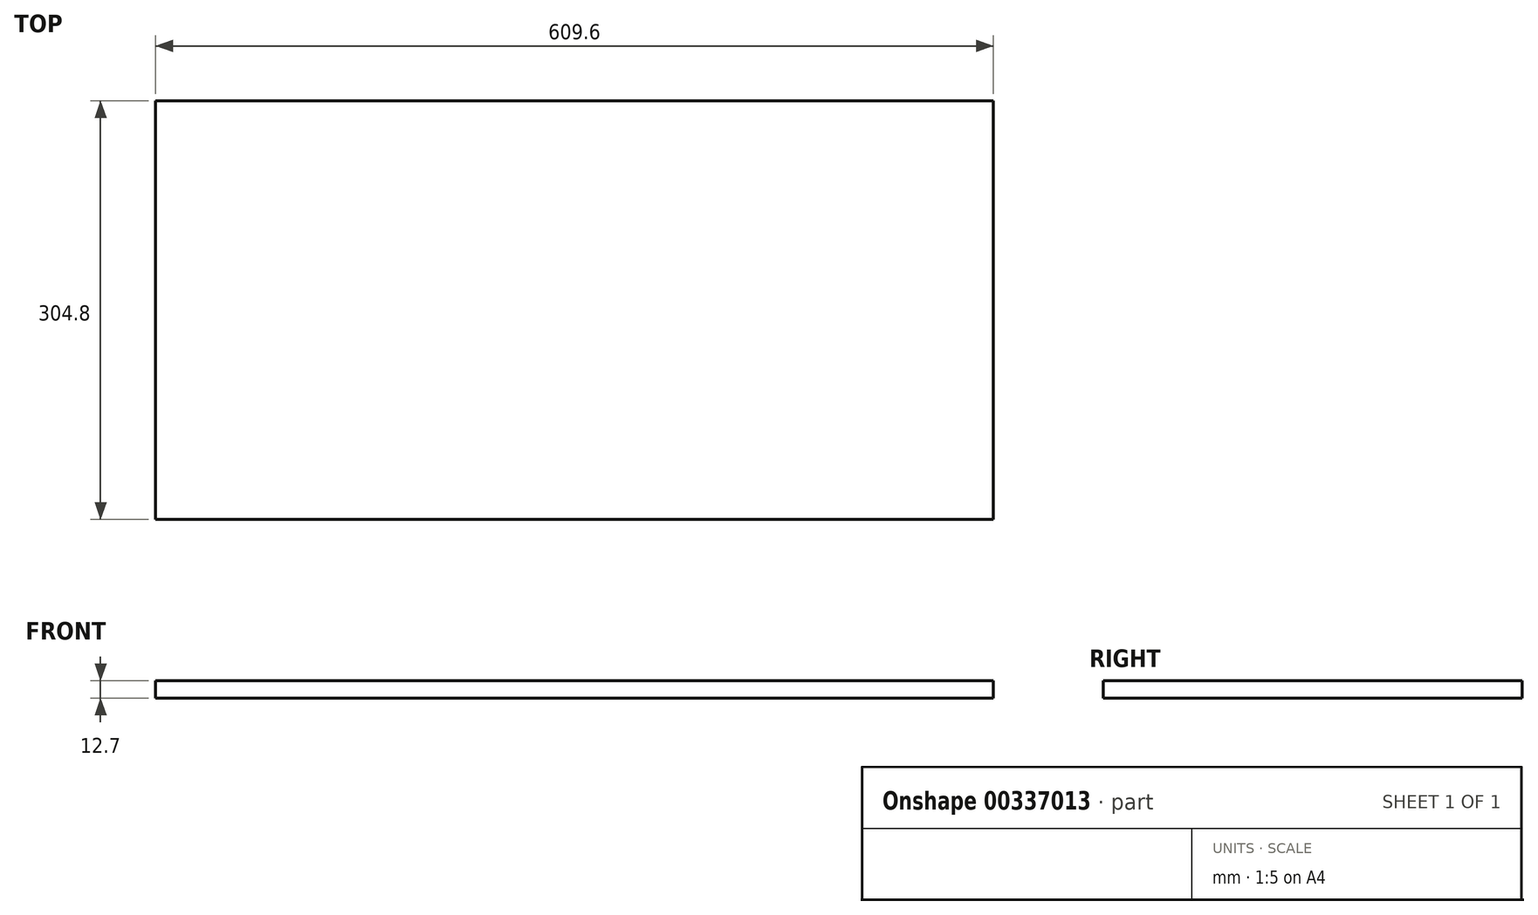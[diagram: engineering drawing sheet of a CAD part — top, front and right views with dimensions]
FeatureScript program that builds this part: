
annotation { "Feature Type Name" : "Feature", "Feature Type Description" : "" }
export const myFeature = defineFeature(function(context is Context, id is Id, definition is map)
    precondition{}
    {
        {
            var Q0;
            Q0=qCreatedBy(makeId("Top.planeOp"),FACE);
            var sketch = newSketch(context, id + "F0", { "sketchPlane" : qUnion([Q0])});
            skLineSegment(sketch, "E0.bottom", {"start": v(-76.53, 265.25) * mm, "end": v(533.07, 265.25) * mm});
            skLineSegment(sketch, "E0.top", {"start": v(-76.53, -39.55) * mm, "end": v(533.07, -39.55) * mm});
            skLineSegment(sketch, "E0.left", {"start": v(-76.53, 265.25) * mm, "end": v(-76.53, -39.55) * mm});
            skLineSegment(sketch, "E0.right", {"start": v(533.07, 265.25) * mm, "end": v(533.07, -39.55) * mm});
            skSolve(sketch);
        }
        {
            var Q0;
            Q0 = qSketchRegion(id + "F0", true);
            extrude(context, id + "F1", {"entities" : qUnion([Q0]), "depth" : 12.7 * mm});
        }
    });
